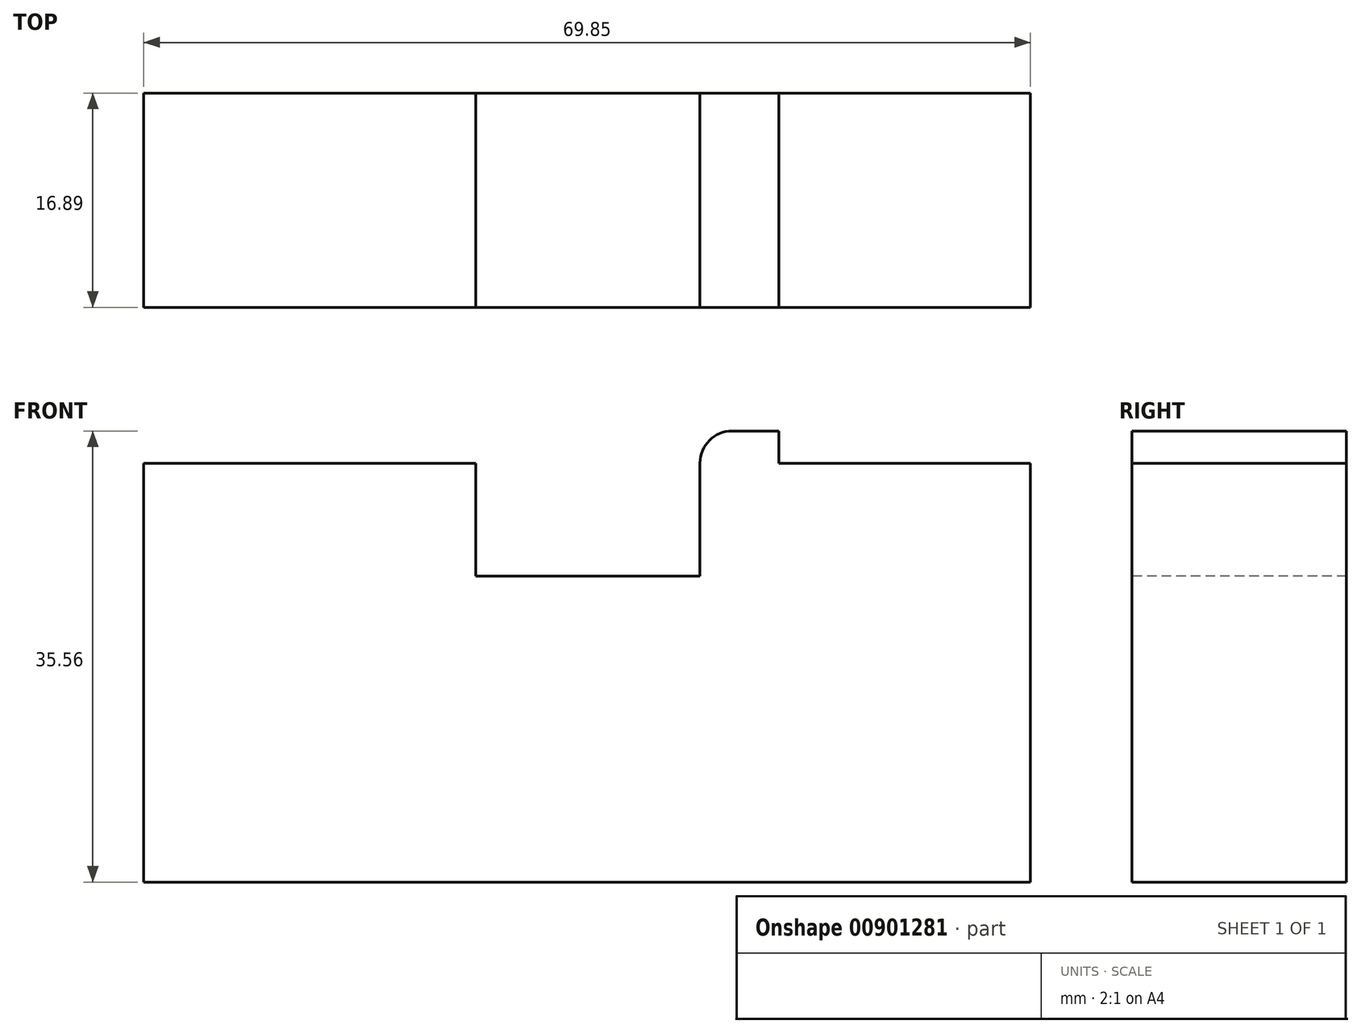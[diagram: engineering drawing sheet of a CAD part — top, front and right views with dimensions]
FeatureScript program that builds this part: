
annotation { "Feature Type Name" : "Feature", "Feature Type Description" : "" }
export const myFeature = defineFeature(function(context is Context, id is Id, definition is map)
    precondition{}
    {
        {
            var Q0;
            Q0=qCreatedBy(makeId("Front.planeOp"),FACE);
            var sketch = newSketch(context, id + "F0", { "sketchPlane" : qUnion([Q0])});
            skLineSegment(sketch, "E0.bottom", {"start": v(0, 0) * mm, "end": v(69.85, 0) * mm});
            skLineSegment(sketch, "E0.top", {"start": v(0, 33.02) * mm, "end": v(69.85, 33.02) * mm});
            skLineSegment(sketch, "E0.left", {"start": v(0, 0) * mm, "end": v(0, 33.02) * mm});
            skLineSegment(sketch, "E0.right", {"start": v(69.85, 0) * mm, "end": v(69.85, 33.02) * mm});
            skSolve(sketch);
        }
        {
            var Q0;
            Q0 = qSketchRegion(id + "F0", true);
            extrude(context, id + "F1", {"entities" : qUnion([Q0]), "depth" : 16.9 * mm, "offsetDistance" : 25.4 * mm});
        }
        {
            var Q0;
            Q0=makeQuery(id+"F1.opExtrude","CAP_FACE",FACE,{"disambiguationData":[OSD([sQuery(id+"F0.wireOp",EDGE,"E0.bottom"),sQuery(id+"F0.wireOp",EDGE,"E0.top"),sQuery(id+"F0.wireOp",EDGE,"E0.left"),sQuery(id+"F0.wireOp",EDGE,"E0.right")])],"isStart":false});
            var sketch = newSketch(context, id + "F2", { "sketchPlane" : qUnion([Q0])});
            skLineSegment(sketch, "E1.bottom", {"start": v(26.16, 33.02) * mm, "end": v(43.82, 33.02) * mm});
            skLineSegment(sketch, "E1.top", {"start": v(26.16, 24.13) * mm, "end": v(43.82, 24.13) * mm});
            skLineSegment(sketch, "E1.left", {"start": v(26.16, 33.02) * mm, "end": v(26.16, 24.13) * mm});
            skLineSegment(sketch, "E1.right", {"start": v(43.82, 33.02) * mm, "end": v(43.82, 24.13) * mm});
            skSolve(sketch);
        }
        {
            var Q0;
            Q0 = qSketchRegion(id + "F2", true);
            extrude(context, id + "F3", {"entities" : qUnion([Q0]), "operationType" : NewBodyOperationType.REMOVE, "oppositeDirection" : true, "depth" : 25.4 * mm, "offsetDistance" : 25.4 * mm});
        }
        {
            var Q0;
            {var subQ0=sQuery(id+"F0.wireOp",EDGE,"E0.right");var subQ2=sQuery(id+"F0.wireOp",EDGE,"E0.top");Q0=makeQuery(id+"F3.boolean.opBoolean","SPLIT",FACE,{"disambiguationData":[TD([makeQuery(id+"F1.opExtrude","SWEPT_FACE",FACE,{"disambiguationData":[OSD([subQ0])]})])],"derivedFrom":makeQuery(id+"F1.opExtrude","SWEPT_FACE",FACE,{"disambiguationData":[OSD([subQ2])]})});}
            var sketch = newSketch(context, id + "F4", { "sketchPlane" : qUnion([Q0])});
            skLineSegment(sketch, "E2.bottom", {"start": v(43.82, 0) * mm, "end": v(50.04, 0) * mm});
            skLineSegment(sketch, "E2.top", {"start": v(43.82, -16.9) * mm, "end": v(50.04, -16.9) * mm});
            skLineSegment(sketch, "E2.left", {"start": v(43.82, 0) * mm, "end": v(43.82, -16.9) * mm});
            skLineSegment(sketch, "E2.right", {"start": v(50.04, 0) * mm, "end": v(50.04, -16.9) * mm});
            skSolve(sketch);
        }
        {
            var Q0;
            Q0 = qSketchRegion(id + "F4", true);
            extrude(context, id + "F5", {"entities" : qUnion([Q0]), "operationType" : NewBodyOperationType.ADD, "depth" : 2.54 * mm, "offsetDistance" : 25.4 * mm});
        }
        {
            var Q0;
            Q0=makeQuery(id+"F5.opExtrude","CAP_EDGE",EDGE,{"disambiguationData":[OSD([sQuery(id+"F4.wireOp",EDGE,"E2.left")])],"isStart":false});
            fillet(context, id + "F6", {"entities" : qUnion([Q0]), "radius" : 2.54 * mm, "tangentPropagation" : true, "allowEdgeOverflow" : false});
        }
    });
